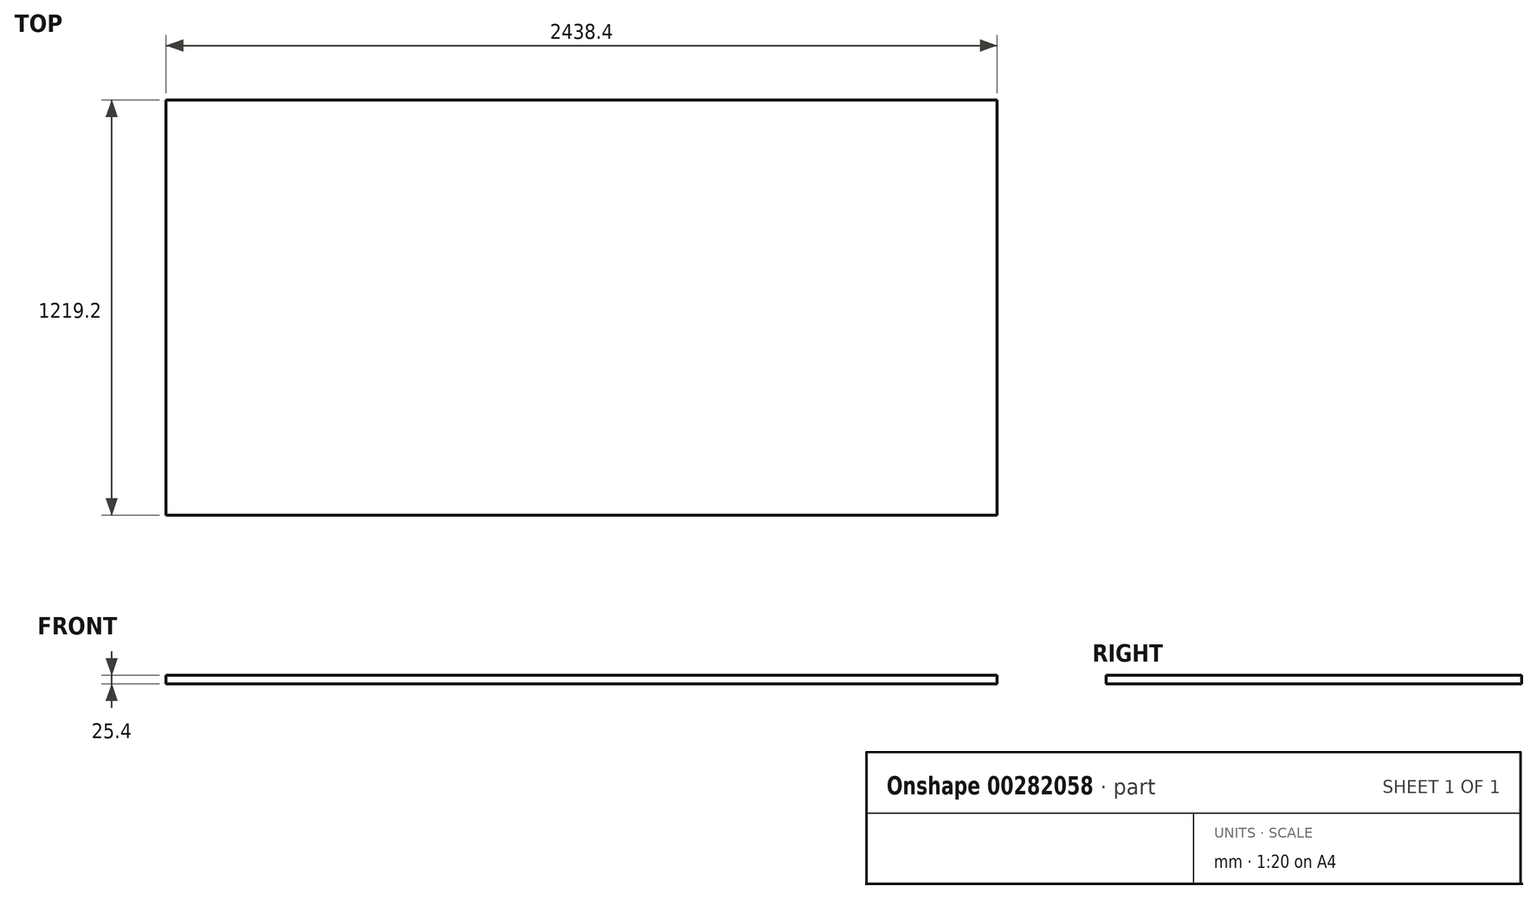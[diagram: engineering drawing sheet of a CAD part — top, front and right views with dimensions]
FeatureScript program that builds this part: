
annotation { "Feature Type Name" : "Feature", "Feature Type Description" : "" }
export const myFeature = defineFeature(function(context is Context, id is Id, definition is map)
    precondition{}
    {
        {
            var Q0;
            Q0=qCreatedBy(makeId("Top.planeOp"), FACE);
            var sketch = newSketch(context, id + "F0", { "sketchPlane" : qUnion([Q0])});
            skLineSegment(sketch, "E0.bottom", {"start": v(0, 0) * mm, "end": v(2438.4, 0) * mm});
            skLineSegment(sketch, "E0.top", {"start": v(0, 1219.2) * mm, "end": v(2438.4, 1219.2) * mm});
            skLineSegment(sketch, "E0.left", {"start": v(0, 0) * mm, "end": v(0, 1219.2) * mm});
            skLineSegment(sketch, "E0.right", {"start": v(2438.4, 0) * mm, "end": v(2438.4, 1219.2) * mm});
            skSolve(sketch);
        }
        {
            var Q0;
            Q0 = qSketchRegion(id + "F0", true);
            extrude(context, id + "F1", {"entities" : qUnion([Q0]), "depth" : 25.4 * mm, "offsetDistance" : 25.4 * mm});
        }
    });
